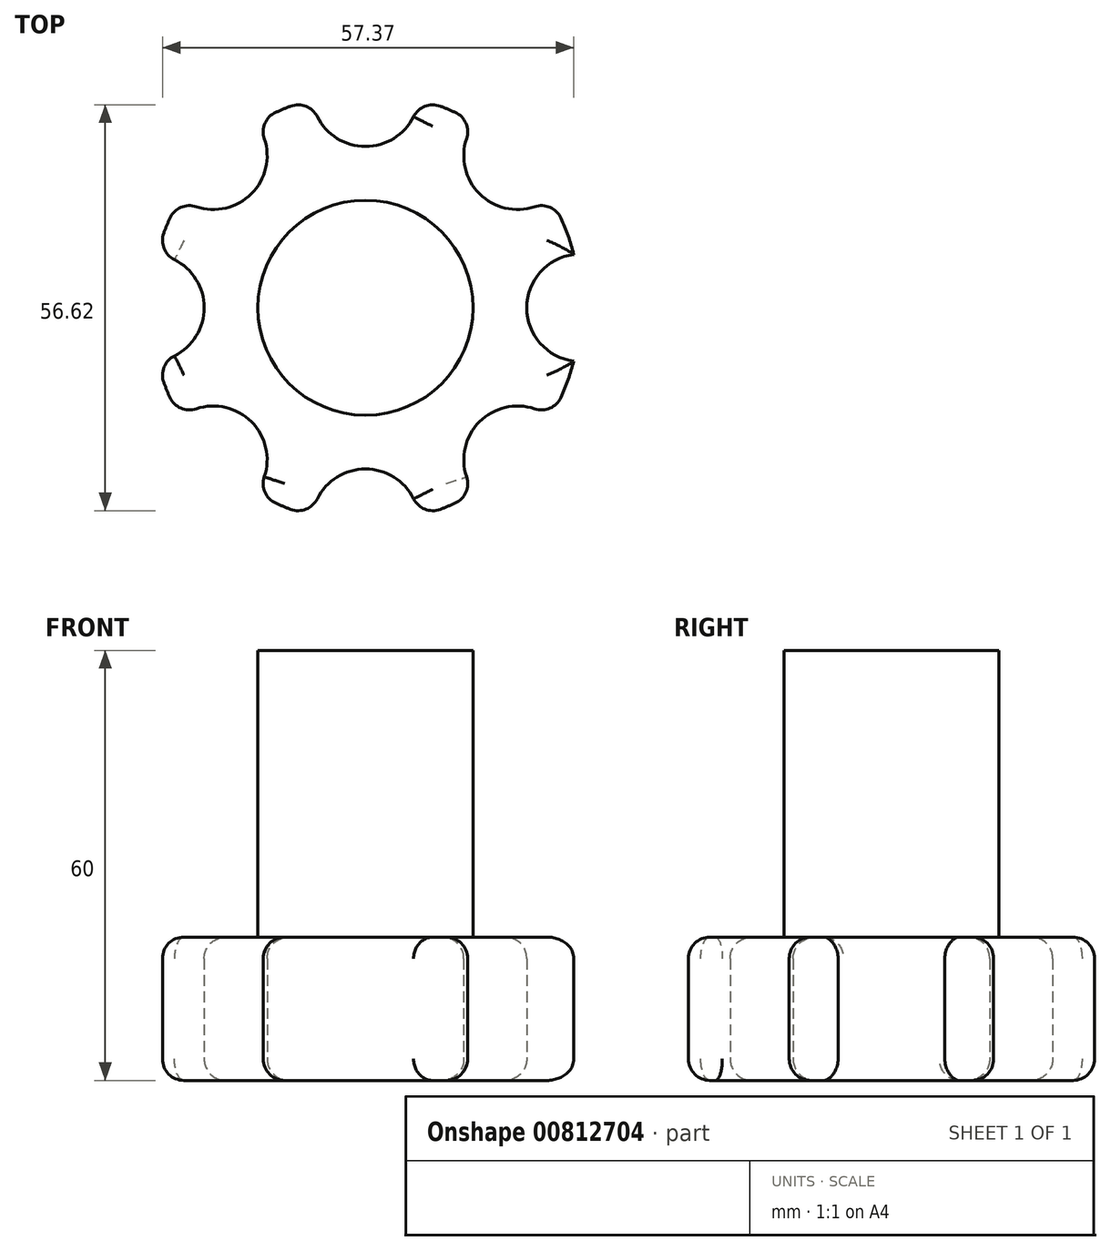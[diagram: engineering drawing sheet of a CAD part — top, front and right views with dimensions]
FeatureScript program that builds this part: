
annotation { "Feature Type Name" : "Feature", "Feature Type Description" : "" }
export const myFeature = defineFeature(function(context is Context, id is Id, definition is map)
    precondition{}
    {
        {
            var Q0;
            Q0=qCreatedBy(makeId("Top.planeOp"),FACE);
            var sketch = newSketch(context, id + "F0", { "sketchPlane" : qUnion([Q0])});
            skCircle(sketch, "E0", {"center": v(0, 0) * mm, "radius": 30 * mm});
            skSolve(sketch);
        }
        {
            var Q0;
            Q0 = qSketchRegion(id + "F0", true);
            extrude(context, id + "F1", {"entities" : qUnion([Q0]), "depth" : 20 * mm, "offsetDistance" : 25 * mm});
        }
        {
            var Q0;
            Q0=makeQuery(id+"F1.opExtrude","CAP_FACE",FACE,{"disambiguationData":[OSD([sQuery(id+"F0.wireOp",EDGE,"E0")])],"isStart":false});
            var sketch = newSketch(context, id + "F2", { "sketchPlane" : qUnion([Q0])});
            skCircle(sketch, "E1", {"center": v(0, 0) * mm, "radius": 15 * mm});
            skSolve(sketch);
        }
        {
            var Q0;
            Q0=makeQuery(id+"F2.imprint","IMPRINT",FACE,{"disambiguationData":[TD([[makeQuery(id+"F2.imprint","IMPRINT",EDGE,{"derivedFrom":sQuery(id+"F2.wireOp",EDGE,"E1")}),1.0]])]});
            extrude(context, id + "F3", {"entities" : qUnion([Q0]), "depth" : 40 * mm, "offsetDistance" : 25 * mm});
        }
        {
            var Q0;
            Q0=makeQuery(id+"F1.opExtrude","CAP_FACE",FACE,{"disambiguationData":[OSD([sQuery(id+"F0.wireOp",EDGE,"E0")])],"isStart":true});
            var sketch = newSketch(context, id + "F4", { "sketchPlane" : qUnion([Q0])});
            skCircle(sketch, "E2", {"center": v(-30, 0) * mm, "radius": 7.5 * mm});
            skCircle(sketch, "E3", {"center": v(-21.21, 21.21) * mm, "radius": 7.5 * mm});
            skCircle(sketch, "E4", {"center": v(0, 30) * mm, "radius": 7.5 * mm});
            skCircle(sketch, "E5", {"center": v(21.21, 21.21) * mm, "radius": 7.5 * mm});
            skCircle(sketch, "E6", {"center": v(30, 0) * mm, "radius": 7.5 * mm});
            skCircle(sketch, "E7", {"center": v(21.21, -21.21) * mm, "radius": 7.5 * mm});
            skCircle(sketch, "E8", {"center": v(0, -30) * mm, "radius": 7.5 * mm});
            skCircle(sketch, "E9", {"center": v(-21.21, -21.21) * mm, "radius": 7.5 * mm});
            skSolve(sketch);
        }
        {
            var Q0;
            Q0 = qSketchRegion(id + "F4", true);
            extrude(context, id + "F5", {"entities" : qUnion([Q0]), "operationType" : NewBodyOperationType.REMOVE, "oppositeDirection" : true, "depth" : 25 * mm, "offsetDistance" : 25 * mm});
        }
        {
            var Q0;
            Q0=makeQuery(id+"F1.opExtrude","CAP_FACE",FACE,{"disambiguationData":[OSD([sQuery(id+"F0.wireOp",EDGE,"E0")])],"isStart":false});
            var Q1;
            Q1=makeQuery(id+"F1.opExtrude","CAP_FACE",FACE,{"disambiguationData":[OSD([sQuery(id+"F0.wireOp",EDGE,"E0")])],"isStart":true});
            var Q2;
            Q2=makeQuery(id+"F5.boolean.opBoolean","COPY",FACE,{"derivedFrom":makeQuery(id+"F5.opExtrude","SWEPT_FACE",FACE,{"disambiguationData":[OSD([sQuery(id+"F4.wireOp",EDGE,"E4")])]})});
            var Q3;
            Q3=makeQuery(id+"F5.boolean.opBoolean","COPY",FACE,{"derivedFrom":makeQuery(id+"F5.opExtrude","SWEPT_FACE",FACE,{"disambiguationData":[OSD([sQuery(id+"F4.wireOp",EDGE,"E5")])]})});
            var Q4;
            Q4=makeQuery(id+"F5.boolean.opBoolean","COPY",FACE,{"derivedFrom":makeQuery(id+"F5.opExtrude","SWEPT_FACE",FACE,{"disambiguationData":[OSD([sQuery(id+"F4.wireOp",EDGE,"E3")])]})});
            var Q5;
            Q5=makeQuery(id+"F5.boolean.opBoolean","COPY",FACE,{"derivedFrom":makeQuery(id+"F5.opExtrude","SWEPT_FACE",FACE,{"disambiguationData":[OSD([sQuery(id+"F4.wireOp",EDGE,"E2")])]})});
            var Q6;
            Q6=makeQuery(id+"F5.boolean.opBoolean","COPY",FACE,{"derivedFrom":makeQuery(id+"F5.opExtrude","SWEPT_FACE",FACE,{"disambiguationData":[OSD([sQuery(id+"F4.wireOp",EDGE,"E9")])]})});
            var Q7;
            Q7=makeQuery(id+"F5.boolean.opBoolean","COPY",FACE,{"derivedFrom":makeQuery(id+"F5.opExtrude","SWEPT_FACE",FACE,{"disambiguationData":[OSD([sQuery(id+"F4.wireOp",EDGE,"E8")])]})});
            var Q8;
            Q8=makeQuery(id+"F5.boolean.opBoolean","COPY",FACE,{"derivedFrom":makeQuery(id+"F5.opExtrude","SWEPT_FACE",FACE,{"disambiguationData":[OSD([sQuery(id+"F4.wireOp",EDGE,"E7")])]})});
            fillet(context, id + "F6", {"entities" : qUnion([Q0, Q1, Q2, Q3, Q4, Q5, Q6, Q7, Q8]), "radius" : 3 * mm, "tangentPropagation" : true, "allowEdgeOverflow" : false});
        }
    });
